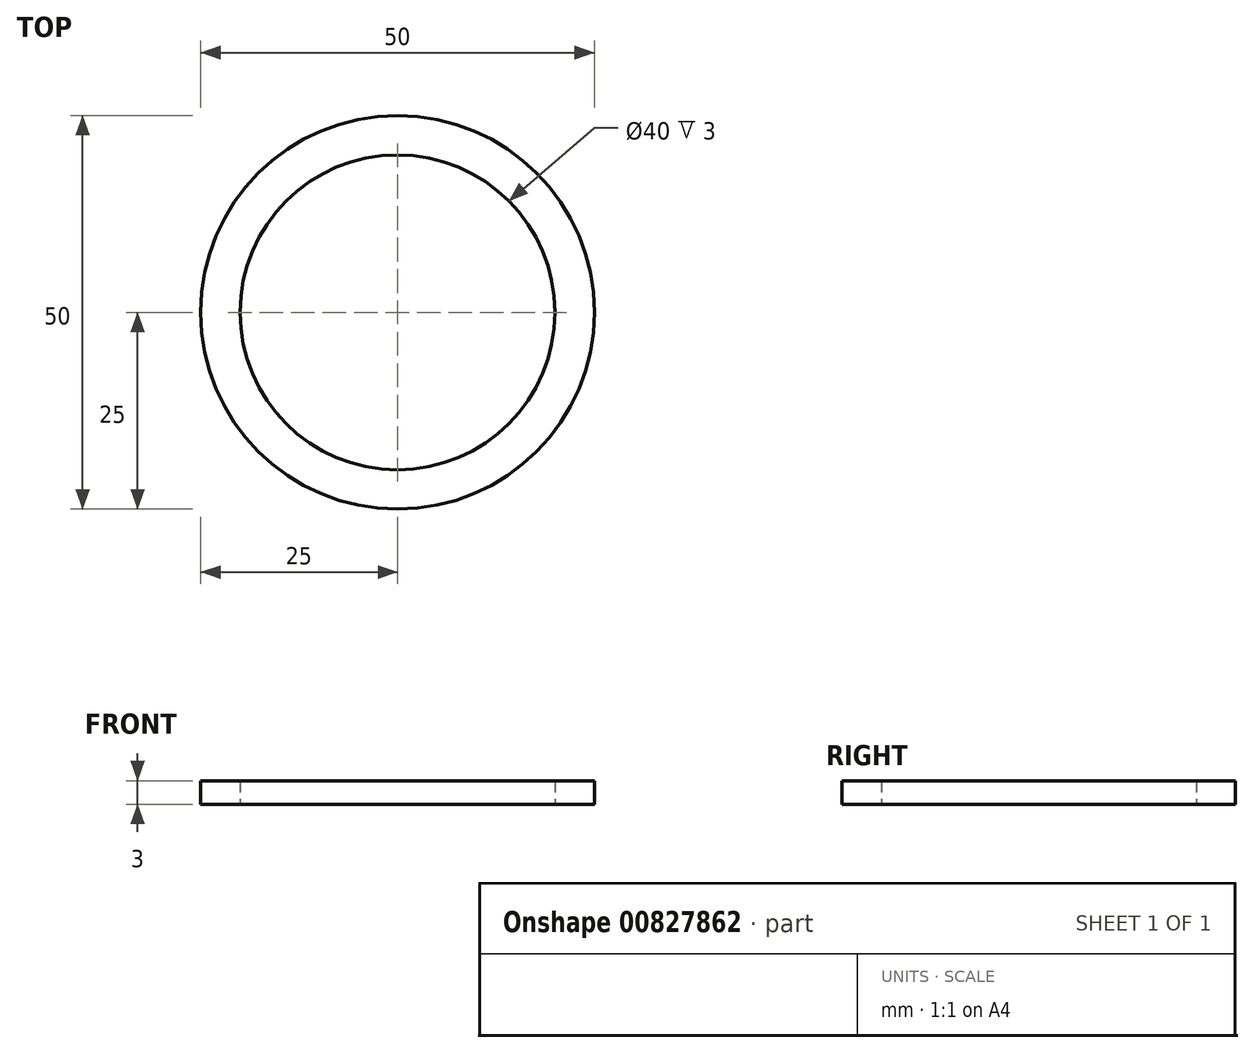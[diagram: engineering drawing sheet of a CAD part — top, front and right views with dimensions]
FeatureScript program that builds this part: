
annotation { "Feature Type Name" : "Feature", "Feature Type Description" : "" }
export const myFeature = defineFeature(function(context is Context, id is Id, definition is map)
    precondition{}
    {
        {
            var Q0;
            Q0=qCreatedBy(makeId("Top.planeOp"),FACE);
            var sketch = newSketch(context, id + "F0", { "sketchPlane" : qUnion([Q0])});
            skCircle(sketch, "E0", {"center": v(0, 0) * mm, "radius": 25 * mm});
            skArc(sketch, "E1", {"start": v(-14.24, -20.55) * mm, "mid": v(10.02, -3.13) * mm, "end": v(0, 25) * mm});
            skCircle(sketch, "E2", {"center": v(0, 0) * mm, "radius": 20 * mm});
            skSolve(sketch);
        }
        {
            var Q0;
            {var subQ0=sQuery(id+"F0.wireOp",EDGE,"E1");var subQ1=sQuery(id+"F0.wireOp",EDGE,"E0");var subQ2=makeQuery(id+"F0.imprint","INTERSECT",VERTEX,{"disambiguationData":[OD(0.0)],"derivedFrom":[subQ1,subQ0]});Q0=makeQuery(id+"F0.imprint","IMPRINT",FACE,{"disambiguationData":[TD([[makeQuery(id+"F0.imprint","IMPRINT",EDGE,{"disambiguationData":[TD([[subQ2,1.0]])],"derivedFrom":subQ1}),1.0]])]});}
            var Q1;
            {var subQ0=sQuery(id+"F0.wireOp",EDGE,"E1");var subQ1=sQuery(id+"F0.wireOp",EDGE,"E0");var subQ2=makeQuery(id+"F0.imprint","INTERSECT",VERTEX,{"disambiguationData":[OD(0.0)],"derivedFrom":[subQ1,subQ0]});Q1=makeQuery(id+"F0.imprint","IMPRINT",FACE,{"disambiguationData":[TD([[makeQuery(id+"F0.imprint","IMPRINT",EDGE,{"disambiguationData":[TD([[subQ2,-1.0]])],"derivedFrom":subQ1}),1.0]])]});}
            var Q2;
            {var subQ0=sQuery(id+"F0.wireOp",EDGE,"E2");var subQ1=sQuery(id+"F0.wireOp",EDGE,"E1");var subQ2=makeQuery(id+"F0.imprint","INTERSECT",VERTEX,{"disambiguationData":[OD(0.0)],"derivedFrom":[subQ1,subQ0]});Q2=makeQuery(id+"F0.imprint","IMPRINT",FACE,{"disambiguationData":[TD([[makeQuery(id+"F0.imprint","IMPRINT",EDGE,{"disambiguationData":[TD([[subQ2,-1.0]])],"derivedFrom":subQ1}),-1.0]])]});}
            extrude(context, id + "F1", {"entities" : qUnion([Q0, Q1, Q2]), "depth" : 1 * mm, "offsetDistance" : 25 * mm});
        }
        {
            var Q0;
            {var subQ0=sQuery(id+"F0.wireOp",EDGE,"E2");var subQ1=sQuery(id+"F0.wireOp",EDGE,"E1");var subQ2=makeQuery(id+"F0.imprint","INTERSECT",VERTEX,{"disambiguationData":[OD(0.0)],"derivedFrom":[subQ1,subQ0]});Q0=makeQuery(id+"F0.imprint","IMPRINT",FACE,{"disambiguationData":[TD([[makeQuery(id+"F0.imprint","IMPRINT",EDGE,{"disambiguationData":[TD([[subQ2,-1.0]])],"derivedFrom":subQ1}),-1.0]])]});}
            var Q1;
            {var subQ0=sQuery(id+"F0.wireOp",EDGE,"E1");var subQ1=sQuery(id+"F0.wireOp",EDGE,"E0");var subQ2=makeQuery(id+"F0.imprint","INTERSECT",VERTEX,{"disambiguationData":[OD(0.0)],"derivedFrom":[subQ1,subQ0]});Q1=makeQuery(id+"F0.imprint","IMPRINT",FACE,{"disambiguationData":[TD([[makeQuery(id+"F0.imprint","IMPRINT",EDGE,{"disambiguationData":[TD([[subQ2,-1.0]])],"derivedFrom":subQ1}),1.0]])]});}
            extrude(context, id + "F2", {"entities" : qUnion([Q0, Q1]), "operationType" : NewBodyOperationType.ADD, "depth" : 3 * mm, "offsetDistance" : 25 * mm});
        }
    });
